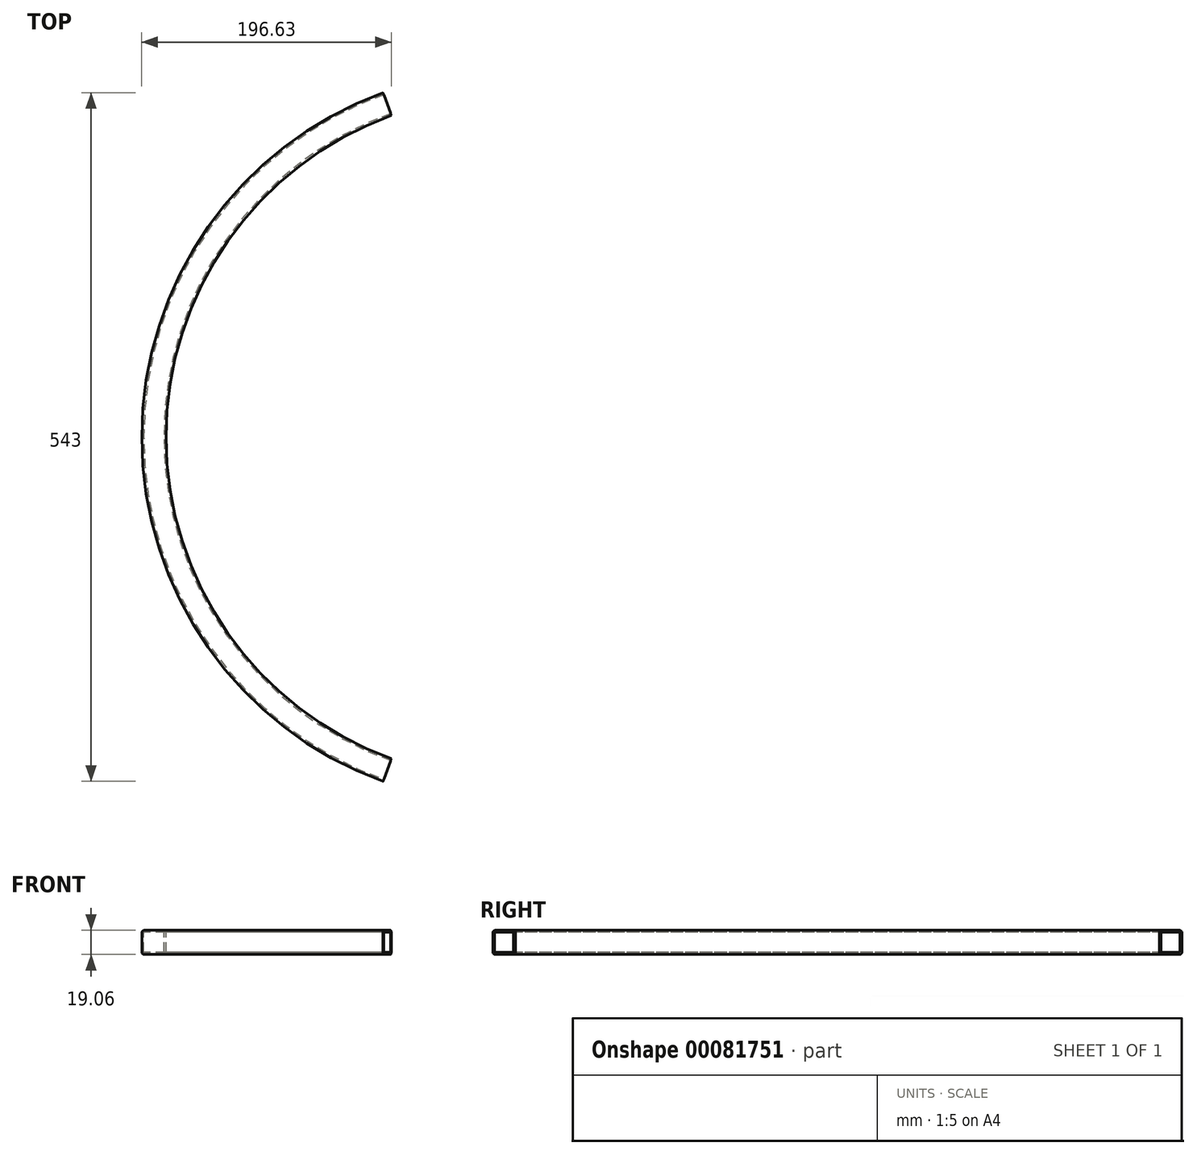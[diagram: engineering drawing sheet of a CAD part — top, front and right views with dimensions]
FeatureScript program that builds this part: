
annotation { "Feature Type Name" : "Feature", "Feature Type Description" : "" }
export const myFeature = defineFeature(function(context is Context, id is Id, definition is map)
    precondition{}
    {
        {
            var Q0;
            Q0=qCreatedBy(makeId("Front.planeOp"),FACE);
            var sketch = newSketch(context, id + "F0", { "sketchPlane" : qUnion([Q0])});
            skLineSegment(sketch, "E0.bottom", {"start": v(7.44, -9.52) * mm, "end": v(-7.44, -9.53) * mm});
            skLineSegment(sketch, "E0.top", {"start": v(7.44, 9.53) * mm, "end": v(-7.44, 9.52) * mm});
            skLineSegment(sketch, "E0.left", {"start": v(9.53, -7.44) * mm, "end": v(9.53, 7.44) * mm});
            skLineSegment(sketch, "E0.right", {"start": v(-9.53, -7.44) * mm, "end": v(-9.53, 7.44) * mm});
            skPoint(sketch, "E0.middle", {"position": v(0, 0) * mm});
            skLineSegment(sketch, "E1.bottom", {"start": v(7.44, -7.95) * mm, "end": v(-7.44, -7.95) * mm});
            skLineSegment(sketch, "E1.top", {"start": v(7.44, 7.95) * mm, "end": v(-7.44, 7.95) * mm});
            skLineSegment(sketch, "E1.left", {"start": v(7.95, -7.44) * mm, "end": v(7.95, 7.44) * mm});
            skLineSegment(sketch, "E1.right", {"start": v(-7.95, -7.44) * mm, "end": v(-7.95, 7.44) * mm});
            skPoint(sketch, "E2.visualSharp", {"position": v(-7.95, 7.95) * mm});
            skArc(sketch, "E2.filletArc", {"start": v(-7.44, 7.95) * mm, "mid": v(-7.8, 7.8) * mm, "end": v(-7.95, 7.44) * mm});
            skPoint(sketch, "E3.visualSharp", {"position": v(7.95, 7.95) * mm});
            skArc(sketch, "E3.filletArc", {"start": v(7.95, 7.44) * mm, "mid": v(7.8, 7.8) * mm, "end": v(7.44, 7.95) * mm});
            skPoint(sketch, "E4.visualSharp", {"position": v(7.95, -7.95) * mm});
            skArc(sketch, "E4.filletArc", {"start": v(7.44, -7.95) * mm, "mid": v(7.8, -7.8) * mm, "end": v(7.95, -7.44) * mm});
            skPoint(sketch, "E5.visualSharp", {"position": v(-7.95, -7.95) * mm});
            skArc(sketch, "E5.filletArc", {"start": v(-7.95, -7.44) * mm, "mid": v(-7.8, -7.8) * mm, "end": v(-7.44, -7.95) * mm});
            skPoint(sketch, "E6.visualSharp", {"position": v(9.53, 9.53) * mm});
            skArc(sketch, "E6.filletArc", {"start": v(9.53, 7.44) * mm, "mid": v(8.91, 8.91) * mm, "end": v(7.44, 9.53) * mm});
            skPoint(sketch, "E7.visualSharp", {"position": v(-9.53, 9.52) * mm});
            skArc(sketch, "E7.filletArc", {"start": v(-7.44, 9.53) * mm, "mid": v(-8.91, 8.91) * mm, "end": v(-9.53, 7.44) * mm});
            skPoint(sketch, "E8.visualSharp", {"position": v(-9.53, -9.53) * mm});
            skArc(sketch, "E8.filletArc", {"start": v(-9.53, -7.44) * mm, "mid": v(-8.91, -8.91) * mm, "end": v(-7.44, -9.52) * mm});
            skPoint(sketch, "E9.visualSharp", {"position": v(9.53, -9.52) * mm});
            skArc(sketch, "E9.filletArc", {"start": v(7.44, -9.52) * mm, "mid": v(8.91, -8.91) * mm, "end": v(9.52, -7.44) * mm});
            skLineSegment(sketch, "E10", {"start": v(279.4, 11.9) * mm, "end": v(279.4, -19.7) * mm});
            skSolve(sketch);
        }
        {
            var Q0;
            Q0 = qSketchRegion(id + "F0", true);
            var Q1;
            Q1=sQuery(id+"F0.wireOp",EDGE,"E10");
            revolve(context, id + "F1", {"entities" : qUnion([Q0]), "axis" : qUnion([Q1]), "revolveType" : RevolveType.SYMMETRIC, "angle" : 140 * degree});
        }
    });
